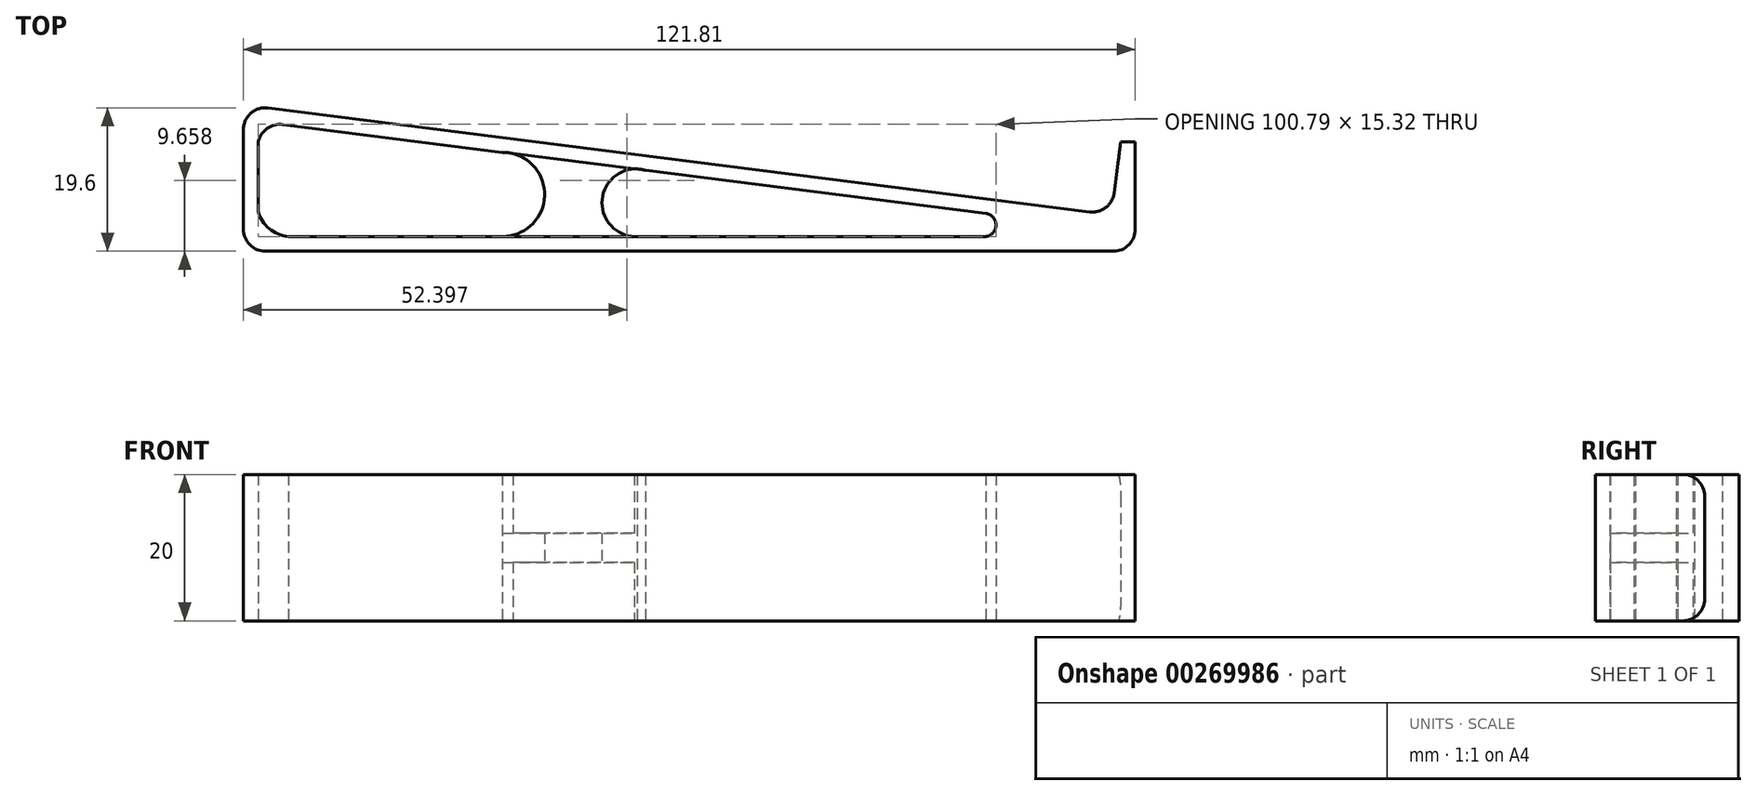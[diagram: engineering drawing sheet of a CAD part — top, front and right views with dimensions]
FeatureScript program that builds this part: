
annotation { "Feature Type Name" : "Feature", "Feature Type Description" : "" }
export const myFeature = defineFeature(function(context is Context, id is Id, definition is map)
    precondition{}
    {
        {
            var Q0;
            Q0=qCreatedBy(makeId("Top.planeOp"),FACE);
            var sketch = newSketch(context, id + "F0", { "sketchPlane" : qUnion([Q0])});
            skLineSegment(sketch, "E0", {"start": v(-59.28, 0) * mm, "end": v(59.28, 0) * mm});
            skLineSegment(sketch, "E1", {"start": v(-59.28, 0) * mm, "end": v(-59.28, 20) * mm});
            skLineSegment(sketch, "E2", {"start": v(-59.28, 20) * mm, "end": v(59.28, 5) * mm});
            skLineSegment(sketch, "E3", {"start": v(59.28, 5) * mm, "end": v(60.53, 14.92) * mm});
            skLineSegment(sketch, "E4", {"start": v(60.53, 14.92) * mm, "end": v(62.53, 14.92) * mm});
            skLineSegment(sketch, "E5", {"start": v(62.53, 14.92) * mm, "end": v(62.53, 0) * mm});
            skLineSegment(sketch, "E6", {"start": v(62.53, 0) * mm, "end": v(59.28, 0) * mm});
            skPoint(sketch, "E7", {"position": v(0, 0) * mm});
            skLineSegment(sketch, "E8", {"start": v(-57.28, 14.94) * mm, "end": v(-57.28, 5.49) * mm});
            skLineSegment(sketch, "E9", {"start": v(-53.1, 2) * mm, "end": v(42.12, 2) * mm});
            skLineSegment(sketch, "E10", {"start": v(42.12, 5.15) * mm, "end": v(-53.89, 17.3) * mm});
            skArc(sketch, "E11", {"start": v(42.12, 2) * mm, "mid": v(43.51, 3.58) * mm, "end": v(42.12, 5.15) * mm});
            skArc(sketch, "E12", {"start": v(-53.87, 17.3) * mm, "mid": v(-56.03, 16.77) * mm, "end": v(-57.28, 14.94) * mm});
            skArc(sketch, "E13", {"start": v(-57.28, 5.49) * mm, "mid": v(-55.76, 3.07) * mm, "end": v(-53.1, 2) * mm});
            skArc(sketch, "E14", {"start": v(-23.89, 2) * mm, "mid": v(-18.14, 7.75) * mm, "end": v(-23.89, 13.5) * mm});
            skPoint(sketch, "E15", {"position": v(-23.89, 13.5) * mm});
            skPoint(sketch, "E16", {"position": v(-23.89, 2) * mm});
            skPoint(sketch, "E17", {"position": v(-5.88, 11.23) * mm});
            skPoint(sketch, "E18", {"position": v(-5.5, 2) * mm});
            skArc(sketch, "E19", {"start": v(-4.35, 11.03) * mm, "mid": v(-10.27, 7.2) * mm, "end": v(-5.5, 2) * mm});
            skSolve(sketch);
        }
        {
            var Q0;
            Q0=makeQuery(id+"F0.imprint","IMPRINT",FACE,{"disambiguationData":[TD([[makeQuery(id+"F0.imprint","IMPRINT",EDGE,{"derivedFrom":sQuery(id+"F0.wireOp",EDGE,"E0")}),1.0]])]});
            extrude(context, id + "F1", {"entities" : qUnion([Q0]), "depth" : 10 * mm, "offsetDistance" : 25 * mm, "hasSecondDirection" : true, "secondDirectionOppositeDirection" : true, "secondDirectionDepth" : 10 * mm});
        }
        {
            var Q0;
            {var subQ0=sQuery(id+"F0.wireOp",EDGE,"E14");var subQ1=sQuery(id+"F0.wireOp",EDGE,"E9");var subQ2=makeQuery(id+"F0.imprint","INTERSECT",VERTEX,{"derivedFrom":[subQ1,subQ0]});Q0=makeQuery(id+"F0.imprint","IMPRINT",FACE,{"disambiguationData":[TD([[makeQuery(id+"F0.imprint","IMPRINT",EDGE,{"disambiguationData":[TD([[subQ2,-1.0]])],"derivedFrom":subQ1}),1.0]])]});}
            extrude(context, id + "F2", {"entities" : qUnion([Q0]), "operationType" : NewBodyOperationType.ADD, "depth" : 2 * mm, "offsetDistance" : 25 * mm, "hasSecondDirection" : true, "secondDirectionOppositeDirection" : true, "secondDirectionDepth" : 2 * mm});
        }
        {
            var Q0;
            Q0=makeQuery(id+"F1.opExtrude","SWEPT_EDGE",EDGE,{"disambiguationData":[OSD([sQuery(id+"F0.wireOp",EDGE,"E5"),sQuery(id+"F0.wireOp",EDGE,"E6")])]});
            var Q1;
            Q1=makeQuery(id+"F1.opExtrude","SWEPT_EDGE",EDGE,{"disambiguationData":[OSD([sQuery(id+"F0.wireOp",EDGE,"E0"),sQuery(id+"F0.wireOp",EDGE,"E1")])]});
            var Q2;
            Q2=makeQuery(id+"F1.opExtrude","SWEPT_EDGE",EDGE,{"disambiguationData":[OSD([sQuery(id+"F0.wireOp",EDGE,"E1"),sQuery(id+"F0.wireOp",EDGE,"E2")])]});
            var Q3;
            Q3=makeQuery(id+"F1.opExtrude","SWEPT_EDGE",EDGE,{"disambiguationData":[OSD([sQuery(id+"F0.wireOp",EDGE,"E2"),sQuery(id+"F0.wireOp",EDGE,"E3")])]});
            var Q4;
            Q4=makeQuery(id+"F1.opExtrude","CAP_EDGE",EDGE,{"disambiguationData":[OSD([sQuery(id+"F0.wireOp",EDGE,"E4")])],"isStart":true});
            var Q5;
            Q5=makeQuery(id+"F1.opExtrude","CAP_EDGE",EDGE,{"disambiguationData":[OSD([sQuery(id+"F0.wireOp",EDGE,"E4")])],"isStart":false});
            fillet(context, id + "F3", {"entities" : qUnion([Q0, Q1, Q2, Q3, Q4, Q5]), "tangentPropagation" : true, "radius" : 3 * mm, "defaultsChanged" : false, "vertexSettings" : [], "allowEdgeOverflow" : false});
        }
    });
